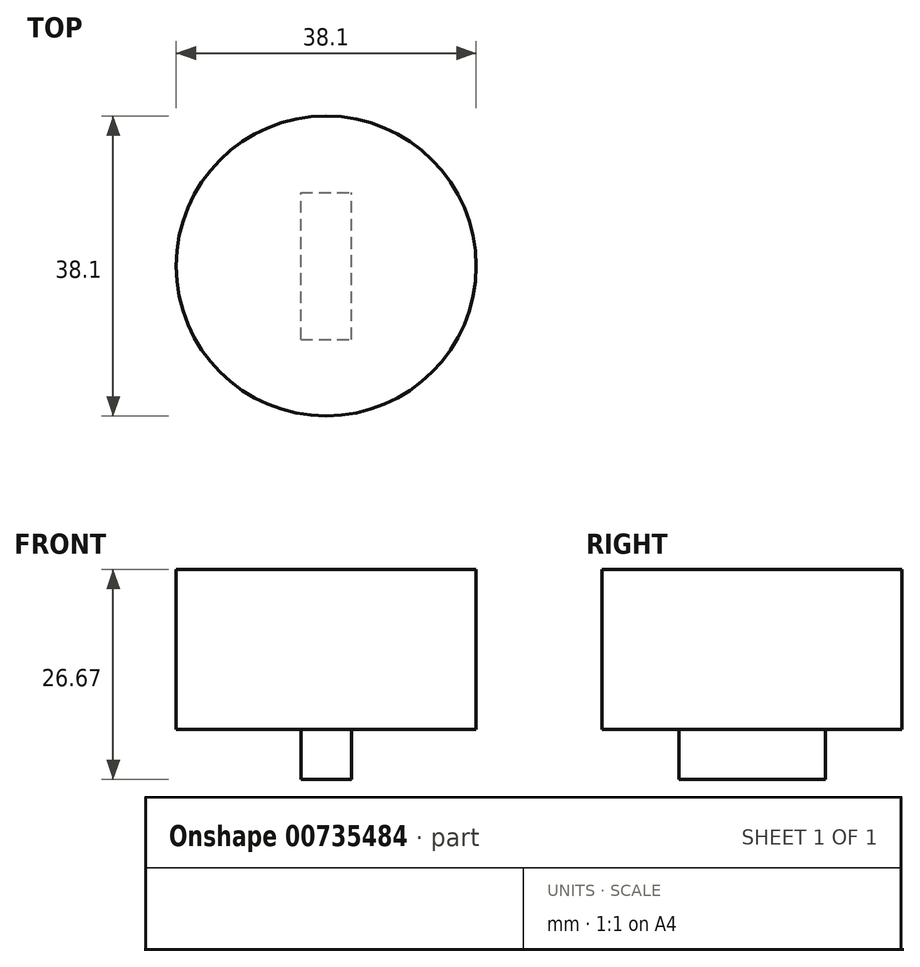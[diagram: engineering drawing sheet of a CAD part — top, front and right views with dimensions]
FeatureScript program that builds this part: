
annotation { "Feature Type Name" : "Feature", "Feature Type Description" : "" }
export const myFeature = defineFeature(function(context is Context, id is Id, definition is map)
    precondition{}
    {
        {
            var Q0;
            Q0=qCreatedBy(makeId("Top.planeOp"),FACE);
            var sketch = newSketch(context, id + "F0", { "sketchPlane" : qUnion([Q0])});
            skCircle(sketch, "E0", {"center": v(0, 0) * mm, "radius": 19.05 * mm});
            skSolve(sketch);
        }
        {
            var Q0;
            Q0=makeQuery(id+"F0.imprint","IMPRINT",FACE,{"disambiguationData":[TD([[makeQuery(id+"F0.imprint","IMPRINT",EDGE,{"derivedFrom":sQuery(id+"F0.wireOp",EDGE,"E0")}),1.0]])]});
            extrude(context, id + "F1", {"entities" : qUnion([Q0]), "depth" : 20.32 * mm, "offsetDistance" : 25.4 * mm});
        }
        {
            var Q0;
            Q0=makeQuery(id+"F1.opExtrude","CAP_FACE",FACE,{"disambiguationData":[OSD([sQuery(id+"F0.wireOp",EDGE,"E0")])],"isStart":true});
            var sketch = newSketch(context, id + "F2", { "sketchPlane" : qUnion([Q0])});
            skLineSegment(sketch, "E1.bottom", {"start": v(-3.2, 9.31) * mm, "end": v(3.2, 9.31) * mm});
            skLineSegment(sketch, "E1.top", {"start": v(-3.2, -9.31) * mm, "end": v(3.2, -9.31) * mm});
            skLineSegment(sketch, "E1.left", {"start": v(-3.2, 9.31) * mm, "end": v(-3.2, -9.31) * mm});
            skLineSegment(sketch, "E1.right", {"start": v(3.2, 9.31) * mm, "end": v(3.2, -9.31) * mm});
            skPoint(sketch, "E1.middle", {"position": v(0, 0) * mm});
            skSolve(sketch);
        }
        {
            var Q0;
            Q0=makeQuery(id+"F2.imprint","IMPRINT",FACE,{"disambiguationData":[TD([[makeQuery(id+"F2.imprint","IMPRINT",EDGE,{"derivedFrom":sQuery(id+"F2.wireOp",EDGE,"E1.bottom")}),-1.0]])]});
            extrude(context, id + "F3", {"entities" : qUnion([Q0]), "operationType" : NewBodyOperationType.ADD, "depth" : 6.35 * mm, "offsetDistance" : 25.4 * mm});
        }
    });
